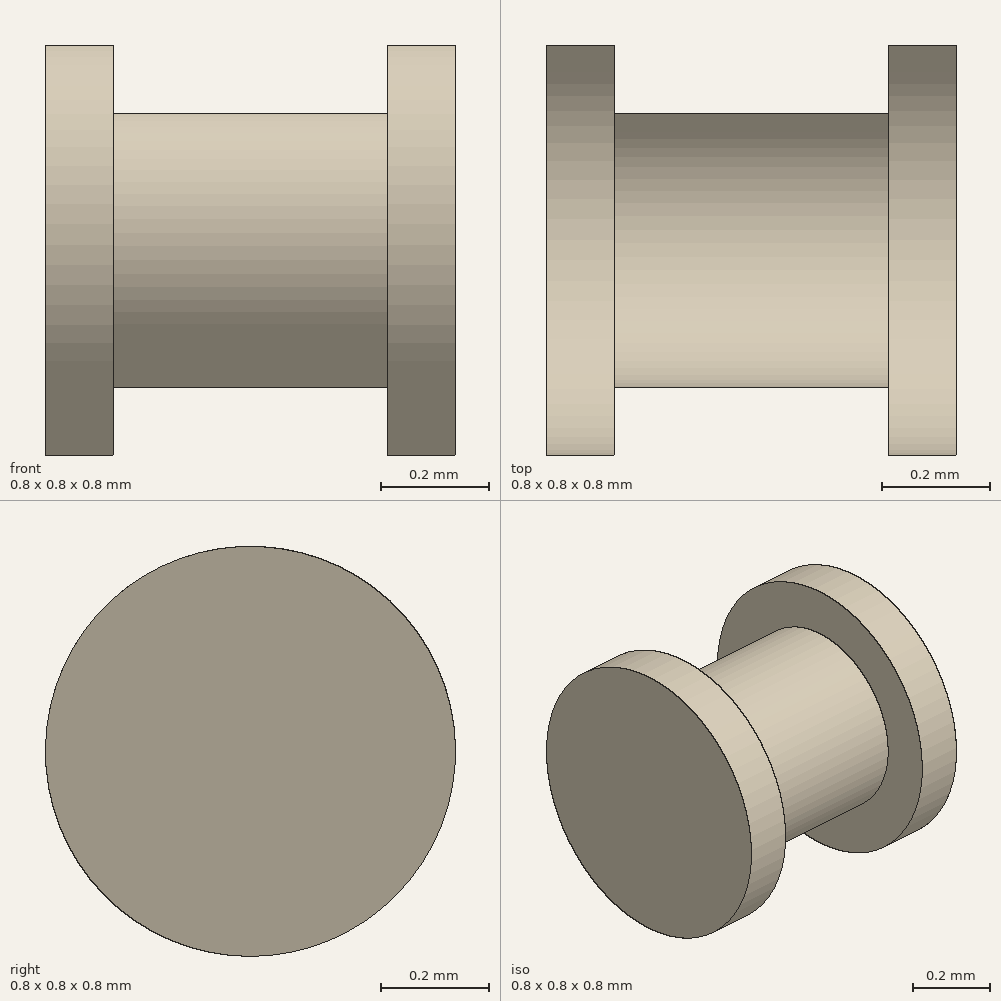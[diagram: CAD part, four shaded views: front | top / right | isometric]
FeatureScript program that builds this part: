
annotation { "Feature Type Name" : "Feature", "Feature Type Description" : "" }
export const myFeature = defineFeature(function(context is Context, id is Id, definition is map)
    precondition{}
    {
        {
            var Q0;
            Q0=qCreatedBy(makeId("Front.planeOp"),FACE);
            var sketch = newSketch(context, id + "F0", { "sketchPlane" : qUnion([Q0])});
            skLineSegment(sketch, "E0", {"start": v(0, 0) * mm, "end": v(0, 0.38) * mm});
            skLineSegment(sketch, "E1", {"start": v(0, 0.38) * mm, "end": v(0.13, 0.38) * mm});
            skLineSegment(sketch, "E2", {"start": v(0.13, 0.38) * mm, "end": v(0.13, 0.25) * mm});
            skLineSegment(sketch, "E3", {"start": v(0.13, 0.25) * mm, "end": v(0.64, 0.25) * mm});
            skLineSegment(sketch, "E4", {"start": v(0.64, 0.25) * mm, "end": v(0.64, 0.38) * mm});
            skLineSegment(sketch, "E5", {"start": v(0.64, 0.38) * mm, "end": v(0.76, 0.38) * mm});
            skLineSegment(sketch, "E6", {"start": v(0.76, 0.38) * mm, "end": v(0.76, 0) * mm});
            skLineSegment(sketch, "E7", {"start": v(0.76, 0) * mm, "end": v(0, 0) * mm});
            skSolve(sketch);
        }
        {
            var Q0;
            Q0 = qSketchRegion(id + "F0", true);
            var Q1;
            Q1=sQuery(id+"F0.wireOp",EDGE,"E7");
            revolve(context, id + "F1", {"entities" : qUnion([Q0]), "axis" : qUnion([Q1]), "revolveType" : RevolveType.FULL});
        }
    });
